# Revit family: QF_Vollrath_72112
name_source: partatom
category: Specialty Equipment
revit_build: Autodesk Revit 2016 (Build: 20151007_0715(x64)
units: mm (PartAtom-declared; Revit-internal decimal feet)

## family parameters
Always vertical = Yes
Cut with Voids When Loaded = No
OmniClass Number = 23.40.40.14.14
OmniClass Title = Food Preparation Equipment
Part Type = Normal
Room Calculation Point = No
Round Connector Dimension = Use Diameter
Shared = No
Work Plane-Based = No

## types (1)
- QF_Vollrath_72112
    Apparent Power = 696 VA
    Assembly Code = E1090320
    CSI MasterFormat = 11 42 00
    Conn Conduit = Yes
    Cycle = 60 Hz
    Description = Drop-In Warmer
    FL Amps = 6 A
    Indirect Waste Size = 1"
    Manufacturer = Vollrath
    Model = 72112
    Number of Poles = 1
    Phase = 1
    URL = www.vollrathco.com
    Volts = 120 V
    Watts = 700 W
    Weight in Pounds = 31.84

## geometry (parser evidence)
native form markers: Blend x18, Sweep x2
no freeform markers — native parametric forms only
